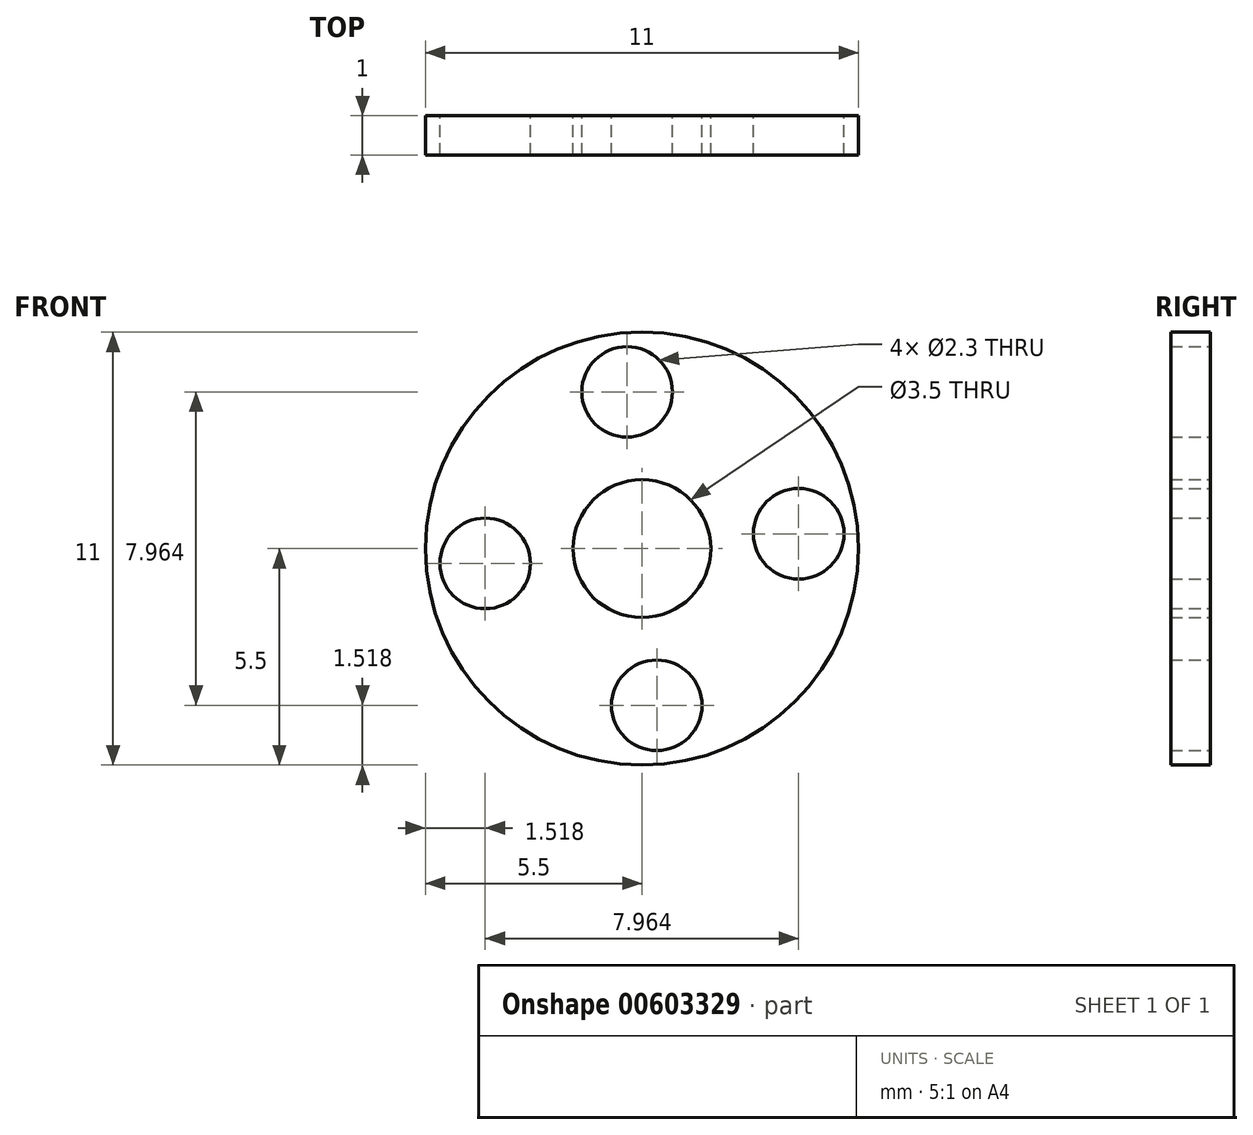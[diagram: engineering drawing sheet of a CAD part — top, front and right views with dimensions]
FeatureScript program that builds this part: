
annotation { "Feature Type Name" : "Feature", "Feature Type Description" : "" }
export const myFeature = defineFeature(function(context is Context, id is Id, definition is map)
    precondition{}
    {
        {
            var Q0;
            Q0=qCreatedBy(makeId("Front.planeOp"),FACE);
            var sketch = newSketch(context, id + "F0", { "sketchPlane" : qUnion([Q0])});
            skCircle(sketch, "E0", {"center": v(0, 0) * mm, "radius": 5.5 * mm});
            skCircle(sketch, "E1", {"center": v(0, 0) * mm, "radius": 1.25 * mm});
            skCircle(sketch, "E2.cCircle", {"center": v(0, 0) * mm, "radius": 4 * mm, "construction": true});
            skCircle(sketch, "E3", {"center": v(0, 0) * mm, "radius": 1.75 * mm});
            skLineSegment(sketch, "E4", {"start": v(-0.52, 5.48) * mm, "end": v(0, 0) * mm});
            skLineSegment(sketch, "E5", {"start": v(0, 0) * mm, "end": v(0.52, -5.48) * mm});
            skLineSegment(sketch, "E6", {"start": v(0, 0) * mm, "end": v(-5.48, -0.52) * mm});
            skLineSegment(sketch, "E7", {"start": v(0, 0) * mm, "end": v(5.48, 0.52) * mm});
            skCircle(sketch, "E8", {"center": v(-3.98, -0.38) * mm, "radius": 1.15 * mm});
            skCircle(sketch, "E9", {"center": v(0.38, -3.98) * mm, "radius": 1.15 * mm});
            skCircle(sketch, "E10", {"center": v(3.98, 0.38) * mm, "radius": 1.15 * mm});
            skCircle(sketch, "E11", {"center": v(-0.38, 3.98) * mm, "radius": 1.15 * mm});
            skCircle(sketch, "E12", {"center": v(0, 0) * mm, "radius": 2.5 * mm});
            skCircle(sketch, "E13", {"center": v(-3.98, -0.38) * mm, "radius": 1.5 * mm});
            skCircle(sketch, "E14", {"center": v(-0.38, 3.98) * mm, "radius": 1.5 * mm});
            skCircle(sketch, "E15", {"center": v(3.98, 0.38) * mm, "radius": 1.5 * mm});
            skCircle(sketch, "E16", {"center": v(0.38, -3.98) * mm, "radius": 1.5 * mm});
            skSolve(sketch);
        }
        {
            var Q0;
            {var subQ0=sQuery(id+"F0.wireOp",EDGE,"E16");var subQ1=sQuery(id+"F0.wireOp",EDGE,"E5");var subQ2=sQuery(id+"F0.wireOp",EDGE,"E0");var subQ3=makeQuery(id+"F0.imprint","INTERSECT",VERTEX,{"derivedFrom":[subQ2,subQ1,subQ0]});Q0=makeQuery(id+"F0.imprint","IMPRINT",FACE,{"disambiguationData":[TD([[makeQuery(id+"F0.imprint","IMPRINT",EDGE,{"disambiguationData":[TD([[subQ3,1.0]])],"derivedFrom":subQ2}),1.0]])]});}
            var Q1;
            {var subQ0=sQuery(id+"F0.wireOp",EDGE,"E14");var subQ1=sQuery(id+"F0.wireOp",EDGE,"E4");var subQ2=sQuery(id+"F0.wireOp",EDGE,"E0");var subQ3=makeQuery(id+"F0.imprint","INTERSECT",VERTEX,{"derivedFrom":[subQ2,subQ1,subQ0]});Q1=makeQuery(id+"F0.imprint","IMPRINT",FACE,{"disambiguationData":[TD([[makeQuery(id+"F0.imprint","IMPRINT",EDGE,{"disambiguationData":[TD([[subQ3,-1.0]])],"derivedFrom":subQ2}),1.0]])]});}
            var Q2;
            {var subQ0=sQuery(id+"F0.wireOp",EDGE,"E14");var subQ1=sQuery(id+"F0.wireOp",EDGE,"E4");var subQ2=sQuery(id+"F0.wireOp",EDGE,"E0");var subQ3=makeQuery(id+"F0.imprint","INTERSECT",VERTEX,{"derivedFrom":[subQ2,subQ1,subQ0]});Q2=makeQuery(id+"F0.imprint","IMPRINT",FACE,{"disambiguationData":[TD([[makeQuery(id+"F0.imprint","IMPRINT",EDGE,{"disambiguationData":[TD([[subQ3,1.0]])],"derivedFrom":subQ2}),1.0]])]});}
            var Q3;
            {var subQ0=sQuery(id+"F0.wireOp",EDGE,"E16");var subQ1=sQuery(id+"F0.wireOp",EDGE,"E5");var subQ2=sQuery(id+"F0.wireOp",EDGE,"E0");var subQ3=makeQuery(id+"F0.imprint","INTERSECT",VERTEX,{"derivedFrom":[subQ2,subQ1,subQ0]});Q3=makeQuery(id+"F0.imprint","IMPRINT",FACE,{"disambiguationData":[TD([[makeQuery(id+"F0.imprint","IMPRINT",EDGE,{"disambiguationData":[TD([[subQ3,-1.0]])],"derivedFrom":subQ2}),1.0]])]});}
            var Q4;
            {var subQ0=sQuery(id+"F0.wireOp",EDGE,"E8");var subQ1=sQuery(id+"F0.wireOp",EDGE,"E6");var subQ2=makeQuery(id+"F0.imprint","INTERSECT",VERTEX,{"disambiguationData":[OD(0.0)],"derivedFrom":[subQ1,subQ0]});Q4=makeQuery(id+"F0.imprint","IMPRINT",FACE,{"disambiguationData":[TD([[makeQuery(id+"F0.imprint","IMPRINT",EDGE,{"disambiguationData":[TD([[subQ2,1.0]])],"derivedFrom":subQ0}),-1.0]])]});}
            var Q5;
            {var subQ0=sQuery(id+"F0.wireOp",EDGE,"E8");var subQ1=sQuery(id+"F0.wireOp",EDGE,"E6");var subQ2=makeQuery(id+"F0.imprint","INTERSECT",VERTEX,{"disambiguationData":[OD(0.0)],"derivedFrom":[subQ1,subQ0]});Q5=makeQuery(id+"F0.imprint","IMPRINT",FACE,{"disambiguationData":[TD([[makeQuery(id+"F0.imprint","IMPRINT",EDGE,{"disambiguationData":[TD([[subQ2,-1.0]])],"derivedFrom":subQ0}),-1.0]])]});}
            var Q6;
            {var subQ1=sQuery(id+"F0.wireOp",EDGE,"E4");var subQ3=sQuery(id+"F0.wireOp",EDGE,"E11");var subQ4=makeQuery(id+"F0.imprint","INTERSECT",VERTEX,{"disambiguationData":[OD(0.0)],"derivedFrom":[subQ1,subQ3]});Q6=makeQuery(id+"F0.imprint","IMPRINT",FACE,{"disambiguationData":[TD([[makeQuery(id+"F0.imprint","IMPRINT",EDGE,{"disambiguationData":[TD([[subQ4,-1.0]])],"derivedFrom":subQ3}),-1.0]])]});}
            var Q7;
            {var subQ1=sQuery(id+"F0.wireOp",EDGE,"E4");var subQ3=sQuery(id+"F0.wireOp",EDGE,"E11");var subQ4=makeQuery(id+"F0.imprint","INTERSECT",VERTEX,{"disambiguationData":[OD(0.0)],"derivedFrom":[subQ1,subQ3]});Q7=makeQuery(id+"F0.imprint","IMPRINT",FACE,{"disambiguationData":[TD([[makeQuery(id+"F0.imprint","IMPRINT",EDGE,{"disambiguationData":[TD([[subQ4,1.0]])],"derivedFrom":subQ3}),-1.0]])]});}
            var Q8;
            {var subQ0=sQuery(id+"F0.wireOp",EDGE,"E9");var subQ1=sQuery(id+"F0.wireOp",EDGE,"E5");var subQ2=makeQuery(id+"F0.imprint","INTERSECT",VERTEX,{"disambiguationData":[OD(0.0)],"derivedFrom":[subQ1,subQ0]});Q8=makeQuery(id+"F0.imprint","IMPRINT",FACE,{"disambiguationData":[TD([[makeQuery(id+"F0.imprint","IMPRINT",EDGE,{"disambiguationData":[TD([[subQ2,1.0]])],"derivedFrom":subQ0}),-1.0]])]});}
            var Q9;
            {var subQ0=sQuery(id+"F0.wireOp",EDGE,"E9");var subQ1=sQuery(id+"F0.wireOp",EDGE,"E5");var subQ2=makeQuery(id+"F0.imprint","INTERSECT",VERTEX,{"disambiguationData":[OD(0.0)],"derivedFrom":[subQ1,subQ0]});Q9=makeQuery(id+"F0.imprint","IMPRINT",FACE,{"disambiguationData":[TD([[makeQuery(id+"F0.imprint","IMPRINT",EDGE,{"disambiguationData":[TD([[subQ2,-1.0]])],"derivedFrom":subQ0}),-1.0]])]});}
            var Q10;
            {var subQ0=sQuery(id+"F0.wireOp",EDGE,"E10");var subQ1=sQuery(id+"F0.wireOp",EDGE,"E7");var subQ2=makeQuery(id+"F0.imprint","INTERSECT",VERTEX,{"disambiguationData":[OD(0.0)],"derivedFrom":[subQ1,subQ0]});Q10=makeQuery(id+"F0.imprint","IMPRINT",FACE,{"disambiguationData":[TD([[makeQuery(id+"F0.imprint","IMPRINT",EDGE,{"disambiguationData":[TD([[subQ2,-1.0]])],"derivedFrom":subQ0}),-1.0]])]});}
            var Q11;
            {var subQ0=sQuery(id+"F0.wireOp",EDGE,"E10");var subQ1=sQuery(id+"F0.wireOp",EDGE,"E7");var subQ2=makeQuery(id+"F0.imprint","INTERSECT",VERTEX,{"disambiguationData":[OD(0.0)],"derivedFrom":[subQ1,subQ0]});Q11=makeQuery(id+"F0.imprint","IMPRINT",FACE,{"disambiguationData":[TD([[makeQuery(id+"F0.imprint","IMPRINT",EDGE,{"disambiguationData":[TD([[subQ2,1.0]])],"derivedFrom":subQ0}),-1.0]])]});}
            var Q12;
            {var subQ0=sQuery(id+"F0.wireOp",EDGE,"E4");var subQ1=sQuery(id+"F0.wireOp",EDGE,"E3");var subQ2=makeQuery(id+"F0.imprint","INTERSECT",VERTEX,{"derivedFrom":[subQ1,subQ0]});Q12=makeQuery(id+"F0.imprint","IMPRINT",FACE,{"disambiguationData":[TD([[makeQuery(id+"F0.imprint","IMPRINT",EDGE,{"disambiguationData":[TD([[subQ2,-1.0]])],"derivedFrom":subQ1}),-1.0]])]});}
            var Q13;
            {var subQ0=sQuery(id+"F0.wireOp",EDGE,"E4");var subQ1=sQuery(id+"F0.wireOp",EDGE,"E3");var subQ2=makeQuery(id+"F0.imprint","INTERSECT",VERTEX,{"derivedFrom":[subQ1,subQ0]});Q13=makeQuery(id+"F0.imprint","IMPRINT",FACE,{"disambiguationData":[TD([[makeQuery(id+"F0.imprint","IMPRINT",EDGE,{"disambiguationData":[TD([[subQ2,1.0]])],"derivedFrom":subQ1}),-1.0]])]});}
            var Q14;
            {var subQ0=sQuery(id+"F0.wireOp",EDGE,"E6");var subQ1=sQuery(id+"F0.wireOp",EDGE,"E3");var subQ2=makeQuery(id+"F0.imprint","INTERSECT",VERTEX,{"derivedFrom":[subQ1,subQ0]});Q14=makeQuery(id+"F0.imprint","IMPRINT",FACE,{"disambiguationData":[TD([[makeQuery(id+"F0.imprint","IMPRINT",EDGE,{"disambiguationData":[TD([[subQ2,-1.0]])],"derivedFrom":subQ1}),-1.0]])]});}
            var Q15;
            {var subQ0=sQuery(id+"F0.wireOp",EDGE,"E7");var subQ1=sQuery(id+"F0.wireOp",EDGE,"E3");var subQ2=makeQuery(id+"F0.imprint","INTERSECT",VERTEX,{"derivedFrom":[subQ1,subQ0]});Q15=makeQuery(id+"F0.imprint","IMPRINT",FACE,{"disambiguationData":[TD([[makeQuery(id+"F0.imprint","IMPRINT",EDGE,{"disambiguationData":[TD([[subQ2,1.0]])],"derivedFrom":subQ1}),-1.0]])]});}
            extrude(context, id + "F1", {"entities" : qUnion([Q0, Q1, Q2, Q3, Q4, Q5, Q6, Q7, Q8, Q9, Q10, Q11, Q12, Q13, Q14, Q15]), "depth" : 1 * mm, "offsetDistance" : 25 * mm});
        }
    });
